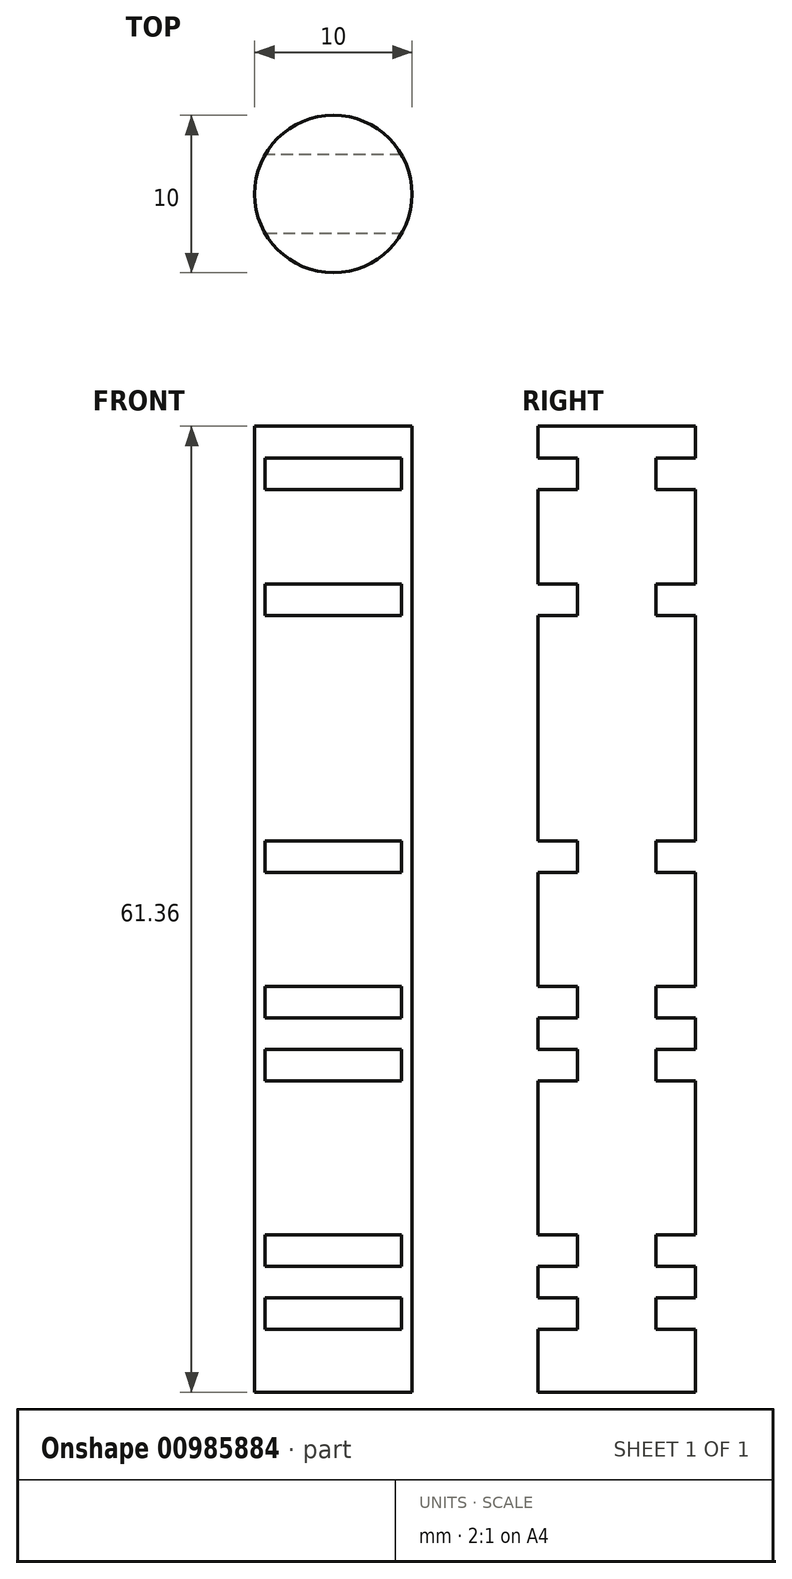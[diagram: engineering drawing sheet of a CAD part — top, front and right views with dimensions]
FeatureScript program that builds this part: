
annotation { "Feature Type Name" : "Feature", "Feature Type Description" : "" }
export const myFeature = defineFeature(function(context is Context, id is Id, definition is map)
    precondition{}
    {
        {
            var Q0;
            Q0=qCreatedBy(makeId("Top.planeOp"),FACE);
            var sketch = newSketch(context, id + "F0", { "sketchPlane" : qUnion([Q0])});
            skCircle(sketch, "E0", {"center": v(0, 0) * mm, "radius": 5 * mm});
            skSolve(sketch);
        }
        {
            var Q0;
            Q0=makeQuery(id+"F0.imprint","IMPRINT",FACE,{"disambiguationData":[TD([[makeQuery(id+"F0.imprint","IMPRINT",EDGE,{"derivedFrom":sQuery(id+"F0.wireOp",EDGE,"E0")}),1.0]])]});
            extrude(context, id + "F1", {"entities" : qUnion([Q0]), "depth" : 2 * mm, "offsetDistance" : 25 * mm});
        }
        {
            var Q0;
            Q0=makeQuery(id+"F1.opExtrude","CAP_FACE",FACE,{"disambiguationData":[OSD([sQuery(id+"F0.wireOp",EDGE,"E0")])],"isStart":true});
            var sketch = newSketch(context, id + "F2", { "sketchPlane" : qUnion([Q0])});
            skPoint(sketch, "E1.middle", {"position": v(0, 0) * mm});
            skArc(sketch, "E2", {"start": v(-4.33, 2.5) * mm, "mid": v(-5, 0) * mm, "end": v(-4.33, -2.5) * mm});
            skArc(sketch, "E3", {"start": v(4.33, -2.5) * mm, "mid": v(5, 0) * mm, "end": v(4.33, 2.5) * mm});
            skLineSegment(sketch, "E4", {"start": v(-4.33, 2.5) * mm, "end": v(4.33, 2.5) * mm});
            skLineSegment(sketch, "E5", {"start": v(4.33, -2.5) * mm, "end": v(-4.33, -2.5) * mm});
            skSolve(sketch);
        }
        {
            var Q0;
            Q0=makeQuery(id+"F2.imprint","IMPRINT",FACE,{"disambiguationData":[TD([[makeQuery(id+"F2.imprint","IMPRINT",EDGE,{"derivedFrom":sQuery(id+"F2.wireOp",EDGE,"E2")}),-1.0]])]});
            extrude(context, id + "F3", {"entities" : qUnion([Q0]), "operationType" : NewBodyOperationType.ADD, "depth" : 2 * mm, "offsetDistance" : 25 * mm});
        }
        {
            var Q0;
            Q0=makeQuery(id+"F3.opExtrude","CAP_FACE",FACE,{"disambiguationData":[OSD([sQuery(id+"F2.wireOp",EDGE,"E2"),sQuery(id+"F2.wireOp",EDGE,"E3"),sQuery(id+"F2.wireOp",EDGE,"E4"),sQuery(id+"F2.wireOp",EDGE,"E5")])],"isStart":false});
            var sketch = newSketch(context, id + "F4", { "sketchPlane" : qUnion([Q0])});
            skCircle(sketch, "E6", {"center": v(0, 0) * mm, "radius": 5 * mm});
            skSolve(sketch);
        }
        {
            var Q0;
            Q0 = qSketchRegion(id + "F4", true);
            extrude(context, id + "F5", {"entities" : qUnion([Q0]), "operationType" : NewBodyOperationType.ADD, "depth" : 6 * mm, "offsetDistance" : 25 * mm});
        }
        {
            var Q0;
            Q0=makeQuery(id+"F5.opExtrude","CAP_FACE",FACE,{"disambiguationData":[OSD([sQuery(id+"F4.wireOp",EDGE,"E6")])],"isStart":false});
            var sketch = newSketch(context, id + "F6", { "sketchPlane" : qUnion([Q0])});
            skLineSegment(sketch, "E7.bottom", {"start": v(6.53, -2.5) * mm, "end": v(-6.53, -2.5) * mm});
            skLineSegment(sketch, "E7.top", {"start": v(6.53, 2.5) * mm, "end": v(-6.53, 2.5) * mm});
            skLineSegment(sketch, "E7.left", {"start": v(6.53, -2.5) * mm, "end": v(6.53, 2.5) * mm});
            skLineSegment(sketch, "E7.right", {"start": v(-6.53, -2.5) * mm, "end": v(-6.53, 2.5) * mm});
            skPoint(sketch, "E7.middle", {"position": v(0, 0) * mm});
            skSolve(sketch);
        }
        {
            var Q0;
            {var subQ0=sQuery(id+"F6.wireOp",EDGE,"E7.bottom");var subQ1=makeQuery(id+"F5.opExtrude","CAP_EDGE",EDGE,{"disambiguationData":[OSD([sQuery(id+"F4.wireOp",EDGE,"E6")])],"isStart":false});var subQ2=makeQuery(id+"F6.imprint","INTERSECT",VERTEX,{"disambiguationData":[OD(0.0)],"derivedFrom":[subQ1,subQ0]});Q0=makeQuery(id+"F6.imprint","IMPRINT",FACE,{"disambiguationData":[TD([[makeQuery(id+"F6.imprint","IMPRINT",EDGE,{"disambiguationData":[TD([[subQ2,-1.0]])],"derivedFrom":subQ0}),-1.0]])]});}
            extrude(context, id + "F7", {"entities" : qUnion([Q0]), "operationType" : NewBodyOperationType.ADD, "depth" : 2 * mm, "offsetDistance" : 25 * mm});
        }
        {
            var Q0;
            Q0=makeQuery(id+"F7.opExtrude","CAP_FACE",FACE,{"disambiguationData":[OSD([sQuery(id+"F4.wireOp",EDGE,"E6"),sQuery(id+"F6.wireOp",EDGE,"E7.bottom"),sQuery(id+"F6.wireOp",EDGE,"E7.top")])],"isStart":false});
            var sketch = newSketch(context, id + "F8", { "sketchPlane" : qUnion([Q0])});
            skCircle(sketch, "E8", {"center": v(0, 0) * mm, "radius": 5 * mm});
            skSolve(sketch);
        }
        {
            var Q0;
            Q0 = qSketchRegion(id + "F8", true);
            extrude(context, id + "F9", {"entities" : qUnion([Q0]), "operationType" : NewBodyOperationType.ADD, "depth" : 14.35 * mm, "offsetDistance" : 25 * mm});
        }
        {
            var Q0;
            Q0=makeQuery(id+"F9.opExtrude","CAP_FACE",FACE,{"disambiguationData":[OSD([sQuery(id+"F8.wireOp",EDGE,"E8")])],"isStart":false});
            var sketch = newSketch(context, id + "F10", { "sketchPlane" : qUnion([Q0])});
            skLineSegment(sketch, "E9.bottom", {"start": v(8.23, -2.5) * mm, "end": v(-8.23, -2.5) * mm});
            skLineSegment(sketch, "E9.top", {"start": v(8.23, 2.5) * mm, "end": v(-8.23, 2.5) * mm});
            skLineSegment(sketch, "E9.left", {"start": v(8.23, -2.5) * mm, "end": v(8.23, 2.5) * mm});
            skLineSegment(sketch, "E9.right", {"start": v(-8.23, -2.5) * mm, "end": v(-8.23, 2.5) * mm});
            skPoint(sketch, "E9.middle", {"position": v(0, 0) * mm});
            skSolve(sketch);
        }
        {
            var Q0;
            {var subQ0=sQuery(id+"F10.wireOp",EDGE,"E9.bottom");var subQ1=makeQuery(id+"F9.opExtrude","CAP_EDGE",EDGE,{"disambiguationData":[OSD([sQuery(id+"F8.wireOp",EDGE,"E8")])],"isStart":false});var subQ2=makeQuery(id+"F10.imprint","INTERSECT",VERTEX,{"disambiguationData":[OD(0.0)],"derivedFrom":[subQ1,subQ0]});Q0=makeQuery(id+"F10.imprint","IMPRINT",FACE,{"disambiguationData":[TD([[makeQuery(id+"F10.imprint","IMPRINT",EDGE,{"disambiguationData":[TD([[subQ2,-1.0]])],"derivedFrom":subQ0}),-1.0]])]});}
            extrude(context, id + "F11", {"entities" : qUnion([Q0]), "operationType" : NewBodyOperationType.ADD, "depth" : 2 * mm, "offsetDistance" : 25 * mm});
        }
        {
            var Q0;
            Q0=makeQuery(id+"F11.opExtrude","CAP_FACE",FACE,{"disambiguationData":[OSD([sQuery(id+"F8.wireOp",EDGE,"E8"),sQuery(id+"F10.wireOp",EDGE,"E9.bottom"),sQuery(id+"F10.wireOp",EDGE,"E9.top")])],"isStart":false});
            var sketch = newSketch(context, id + "F12", { "sketchPlane" : qUnion([Q0])});
            skCircle(sketch, "E10", {"center": v(0, 0) * mm, "radius": 5 * mm});
            skSolve(sketch);
        }
        {
            var Q0;
            Q0 = qSketchRegion(id + "F12", true);
            extrude(context, id + "F13", {"entities" : qUnion([Q0]), "operationType" : NewBodyOperationType.ADD, "depth" : 7.22 * mm, "offsetDistance" : 25 * mm});
        }
        {
            var Q0;
            Q0=makeQuery(id+"F13.opExtrude","CAP_FACE",FACE,{"disambiguationData":[OSD([sQuery(id+"F12.wireOp",EDGE,"E10")])],"isStart":false});
            var sketch = newSketch(context, id + "F14", { "sketchPlane" : qUnion([Q0])});
            skLineSegment(sketch, "E11.bottom", {"start": v(9.26, -2.5) * mm, "end": v(-9.26, -2.5) * mm});
            skLineSegment(sketch, "E11.top", {"start": v(9.26, 2.5) * mm, "end": v(-9.26, 2.5) * mm});
            skLineSegment(sketch, "E11.left", {"start": v(9.26, -2.5) * mm, "end": v(9.26, 2.5) * mm});
            skLineSegment(sketch, "E11.right", {"start": v(-9.26, -2.5) * mm, "end": v(-9.26, 2.5) * mm});
            skPoint(sketch, "E11.middle", {"position": v(0, 0) * mm});
            skSolve(sketch);
        }
        {
            var Q0;
            {var subQ0=sQuery(id+"F14.wireOp",EDGE,"E11.bottom");var subQ1=makeQuery(id+"F13.opExtrude","CAP_EDGE",EDGE,{"disambiguationData":[OSD([sQuery(id+"F12.wireOp",EDGE,"E10")])],"isStart":false});var subQ2=makeQuery(id+"F14.imprint","INTERSECT",VERTEX,{"disambiguationData":[OD(0.0)],"derivedFrom":[subQ1,subQ0]});Q0=makeQuery(id+"F14.imprint","IMPRINT",FACE,{"disambiguationData":[TD([[makeQuery(id+"F14.imprint","IMPRINT",EDGE,{"disambiguationData":[TD([[subQ2,-1.0]])],"derivedFrom":subQ0}),-1.0]])]});}
            extrude(context, id + "F15", {"entities" : qUnion([Q0]), "operationType" : NewBodyOperationType.ADD, "depth" : 2 * mm, "offsetDistance" : 25 * mm});
        }
        {
            var Q0;
            Q0=makeQuery(id+"F15.opExtrude","CAP_FACE",FACE,{"disambiguationData":[OSD([sQuery(id+"F12.wireOp",EDGE,"E10"),sQuery(id+"F14.wireOp",EDGE,"E11.bottom"),sQuery(id+"F14.wireOp",EDGE,"E11.top")])],"isStart":false});
            var sketch = newSketch(context, id + "F16", { "sketchPlane" : qUnion([Q0])});
            skCircle(sketch, "E12", {"center": v(0, 0) * mm, "radius": 5 * mm});
            skSolve(sketch);
        }
        {
            var Q0;
            Q0 = qSketchRegion(id + "F16", true);
            extrude(context, id + "F17", {"entities" : qUnion([Q0]), "operationType" : NewBodyOperationType.ADD, "depth" : 2 * mm, "offsetDistance" : 25 * mm});
        }
        {
            var Q0;
            Q0=makeQuery(id+"F17.opExtrude","CAP_FACE",FACE,{"disambiguationData":[OSD([sQuery(id+"F16.wireOp",EDGE,"E12")])],"isStart":false});
            var sketch = newSketch(context, id + "F18", { "sketchPlane" : qUnion([Q0])});
            skLineSegment(sketch, "E13.bottom", {"start": v(6.32, -2.5) * mm, "end": v(-6.32, -2.5) * mm});
            skLineSegment(sketch, "E13.top", {"start": v(6.32, 2.5) * mm, "end": v(-6.32, 2.5) * mm});
            skLineSegment(sketch, "E13.left", {"start": v(6.32, -2.5) * mm, "end": v(6.32, 2.5) * mm});
            skLineSegment(sketch, "E13.right", {"start": v(-6.32, -2.5) * mm, "end": v(-6.32, 2.5) * mm});
            skPoint(sketch, "E13.middle", {"position": v(0, 0) * mm});
            skSolve(sketch);
        }
        {
            var Q0;
            {var subQ0=sQuery(id+"F18.wireOp",EDGE,"E13.bottom");var subQ1=makeQuery(id+"F17.opExtrude","CAP_EDGE",EDGE,{"disambiguationData":[OSD([sQuery(id+"F16.wireOp",EDGE,"E12")])],"isStart":false});var subQ2=makeQuery(id+"F18.imprint","INTERSECT",VERTEX,{"disambiguationData":[OD(0.0)],"derivedFrom":[subQ1,subQ0]});Q0=makeQuery(id+"F18.imprint","IMPRINT",FACE,{"disambiguationData":[TD([[makeQuery(id+"F18.imprint","IMPRINT",EDGE,{"disambiguationData":[TD([[subQ2,-1.0]])],"derivedFrom":subQ0}),-1.0]])]});}
            extrude(context, id + "F19", {"entities" : qUnion([Q0]), "operationType" : NewBodyOperationType.ADD, "depth" : 2 * mm, "offsetDistance" : 25 * mm});
        }
        {
            var Q0;
            Q0=makeQuery(id+"F19.opExtrude","CAP_FACE",FACE,{"disambiguationData":[OSD([sQuery(id+"F16.wireOp",EDGE,"E12"),sQuery(id+"F18.wireOp",EDGE,"E13.bottom"),sQuery(id+"F18.wireOp",EDGE,"E13.top")])],"isStart":false});
            var sketch = newSketch(context, id + "F20", { "sketchPlane" : qUnion([Q0])});
            skCircle(sketch, "E14", {"center": v(0, 0) * mm, "radius": 5 * mm});
            skSolve(sketch);
        }
        {
            var Q0;
            Q0 = qSketchRegion(id + "F20", true);
            extrude(context, id + "F21", {"entities" : qUnion([Q0]), "operationType" : NewBodyOperationType.ADD, "depth" : 9.78 * mm, "offsetDistance" : 25 * mm});
        }
        {
            var Q0;
            Q0=makeQuery(id+"F21.opExtrude","CAP_FACE",FACE,{"disambiguationData":[OSD([sQuery(id+"F20.wireOp",EDGE,"E14")])],"isStart":false});
            var sketch = newSketch(context, id + "F22", { "sketchPlane" : qUnion([Q0])});
            skLineSegment(sketch, "E15.bottom", {"start": v(7.08, -2.5) * mm, "end": v(-7.08, -2.5) * mm});
            skLineSegment(sketch, "E15.top", {"start": v(7.08, 2.5) * mm, "end": v(-7.08, 2.5) * mm});
            skLineSegment(sketch, "E15.left", {"start": v(7.08, -2.5) * mm, "end": v(7.08, 2.5) * mm});
            skLineSegment(sketch, "E15.right", {"start": v(-7.08, -2.5) * mm, "end": v(-7.08, 2.5) * mm});
            skPoint(sketch, "E15.middle", {"position": v(0, 0) * mm});
            skSolve(sketch);
        }
        {
            var Q0;
            {var subQ0=sQuery(id+"F22.wireOp",EDGE,"E15.bottom");var subQ1=makeQuery(id+"F21.opExtrude","CAP_EDGE",EDGE,{"disambiguationData":[OSD([sQuery(id+"F20.wireOp",EDGE,"E14")])],"isStart":false});var subQ2=makeQuery(id+"F22.imprint","INTERSECT",VERTEX,{"disambiguationData":[OD(0.0)],"derivedFrom":[subQ1,subQ0]});Q0=makeQuery(id+"F22.imprint","IMPRINT",FACE,{"disambiguationData":[TD([[makeQuery(id+"F22.imprint","IMPRINT",EDGE,{"disambiguationData":[TD([[subQ2,-1.0]])],"derivedFrom":subQ0}),-1.0]])]});}
            extrude(context, id + "F23", {"entities" : qUnion([Q0]), "operationType" : NewBodyOperationType.ADD, "depth" : 2 * mm, "offsetDistance" : 25 * mm});
        }
        {
            var Q0;
            Q0=makeQuery(id+"F23.opExtrude","CAP_FACE",FACE,{"disambiguationData":[OSD([sQuery(id+"F20.wireOp",EDGE,"E14"),sQuery(id+"F22.wireOp",EDGE,"E15.bottom"),sQuery(id+"F22.wireOp",EDGE,"E15.top")])],"isStart":false});
            var sketch = newSketch(context, id + "F24", { "sketchPlane" : qUnion([Q0])});
            skCircle(sketch, "E16", {"center": v(0, 0) * mm, "radius": 5 * mm});
            skSolve(sketch);
        }
        {
            var Q0;
            Q0 = qSketchRegion(id + "F24", true);
            extrude(context, id + "F25", {"entities" : qUnion([Q0]), "operationType" : NewBodyOperationType.ADD, "depth" : 2 * mm, "offsetDistance" : 25 * mm});
        }
        {
            var Q0;
            Q0=makeQuery(id+"F25.opExtrude","CAP_FACE",FACE,{"disambiguationData":[OSD([sQuery(id+"F24.wireOp",EDGE,"E16")])],"isStart":false});
            var sketch = newSketch(context, id + "F26", { "sketchPlane" : qUnion([Q0])});
            skSolve(sketch);
        }
        {
            var Q0;
            Q0=makeQuery(id+"F26.imprint","IMPRINT",FACE,{"disambiguationData":[TD([[makeQuery(id+"F26.imprint","IMPRINT",EDGE,{"derivedFrom":makeQuery(id+"F25.opExtrude","CAP_EDGE",EDGE,{"disambiguationData":[OSD([sQuery(id+"F24.wireOp",EDGE,"E16")])],"isStart":false})}),1.0]])]});
            var sketch = newSketch(context, id + "F27", { "sketchPlane" : qUnion([Q0])});
            skLineSegment(sketch, "E17.bottom", {"start": v(8.5, -2.5) * mm, "end": v(-8.5, -2.5) * mm});
            skLineSegment(sketch, "E17.top", {"start": v(8.5, 2.5) * mm, "end": v(-8.5, 2.5) * mm});
            skLineSegment(sketch, "E17.left", {"start": v(8.5, -2.5) * mm, "end": v(8.5, 2.5) * mm});
            skLineSegment(sketch, "E17.right", {"start": v(-8.5, -2.5) * mm, "end": v(-8.5, 2.5) * mm});
            skPoint(sketch, "E17.middle", {"position": v(0, 0) * mm});
            skSolve(sketch);
        }
        {
            var Q0;
            {var subQ0=sQuery(id+"F27.wireOp",EDGE,"E17.bottom");var subQ1=makeQuery(id+"F26.imprint","IMPRINT",EDGE,{"derivedFrom":makeQuery(id+"F25.opExtrude","CAP_EDGE",EDGE,{"disambiguationData":[OSD([sQuery(id+"F24.wireOp",EDGE,"E16")])],"isStart":false})});var subQ2=makeQuery(id+"F27.imprint","INTERSECT",VERTEX,{"disambiguationData":[OD(0.0)],"derivedFrom":[subQ1,subQ0]});Q0=makeQuery(id+"F27.imprint","IMPRINT",FACE,{"disambiguationData":[TD([[makeQuery(id+"F27.imprint","IMPRINT",EDGE,{"disambiguationData":[TD([[subQ2,-1.0]])],"derivedFrom":subQ0}),-1.0]])]});}
            extrude(context, id + "F28", {"entities" : qUnion([Q0]), "operationType" : NewBodyOperationType.ADD, "depth" : 2 * mm, "offsetDistance" : 25 * mm});
        }
        {
            var Q0;
            Q0=makeQuery(id+"F28.opExtrude","CAP_FACE",FACE,{"disambiguationData":[OSD([sQuery(id+"F24.wireOp",EDGE,"E16"),sQuery(id+"F27.wireOp",EDGE,"E17.bottom"),sQuery(id+"F27.wireOp",EDGE,"E17.top")])],"isStart":false});
            var sketch = newSketch(context, id + "F29", { "sketchPlane" : qUnion([Q0])});
            skCircle(sketch, "E18", {"center": v(0, 0) * mm, "radius": 5 * mm});
            skSolve(sketch);
        }
        {
            var Q0;
            Q0 = qSketchRegion(id + "F29", true);
            extrude(context, id + "F30", {"entities" : qUnion([Q0]), "operationType" : NewBodyOperationType.ADD, "depth" : 4 * mm, "offsetDistance" : 25 * mm});
        }
    });
